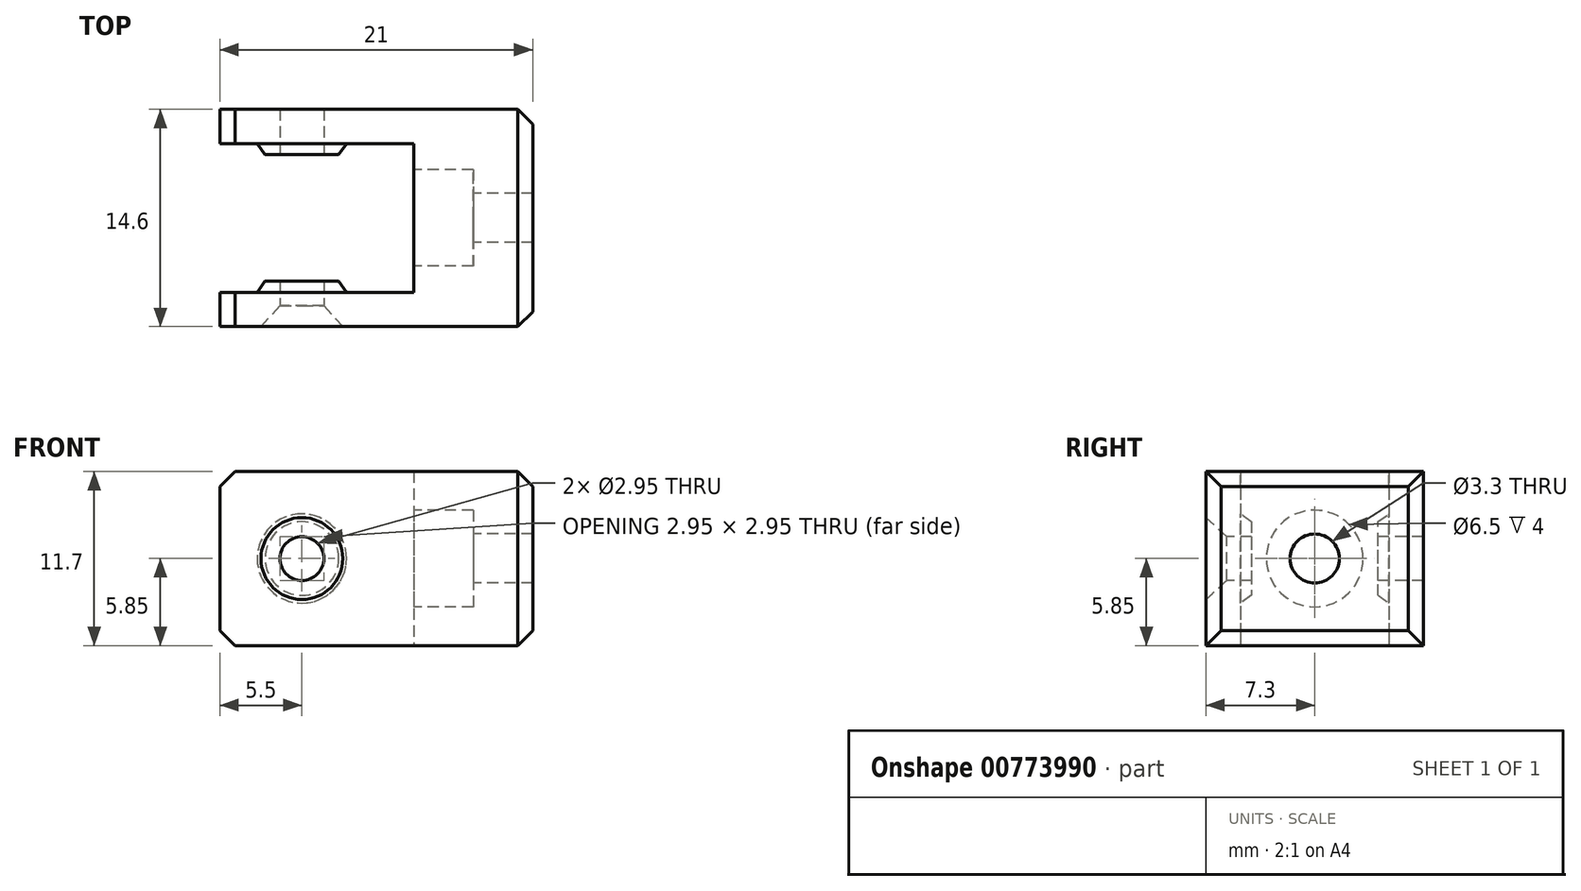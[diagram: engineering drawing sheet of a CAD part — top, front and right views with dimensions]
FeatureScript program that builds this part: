
annotation { "Feature Type Name" : "Feature", "Feature Type Description" : "" }
export const myFeature = defineFeature(function(context is Context, id is Id, definition is map)
    precondition{}
    {
        {
            var Q0;
            Q0=qCreatedBy(makeId("Top.planeOp"),FACE);
            var sketch = newSketch(context, id + "F0", { "sketchPlane" : qUnion([Q0])});
            skLineSegment(sketch, "E0", {"start": v(8, -7.3) * mm, "end": v(8, 0) * mm});
            skLineSegment(sketch, "E1", {"start": v(8, 0) * mm, "end": v(0, 0) * mm});
            skLineSegment(sketch, "E2", {"start": v(0, 0) * mm, "end": v(0, -5) * mm});
            skLineSegment(sketch, "E3", {"start": v(0, -5) * mm, "end": v(-13, -5) * mm});
            skLineSegment(sketch, "E4", {"start": v(-13, -5) * mm, "end": v(-13, -7.3) * mm});
            skLineSegment(sketch, "E5", {"start": v(-13, -7.3) * mm, "end": v(8, -7.3) * mm});
            skLineSegment(sketch, "E6.MirrorCS", {"start": v(0, 0) * mm, "end": v(0, 5) * mm});
            skLineSegment(sketch, "E7.MirrorCS", {"start": v(-13, 7.3) * mm, "end": v(8, 7.3) * mm});
            skLineSegment(sketch, "E8.MirrorCS", {"start": v(8, 7.3) * mm, "end": v(8, 0) * mm});
            skLineSegment(sketch, "E9.MirrorCS", {"start": v(0, 5) * mm, "end": v(-13, 5) * mm});
            skLineSegment(sketch, "E10.MirrorCS", {"start": v(-13, 5) * mm, "end": v(-13, 7.3) * mm});
            skSolve(sketch);
        }
        {
            var Q0;
            Q0 = qSketchRegion(id + "F0", true);
            extrude(context, id + "F1", {"entities" : qUnion([Q0]), "depth" : 11.7 * mm, "offsetDistance" : 25 * mm});
        }
        {
            var Q0;
            Q0=makeQuery(id+"F1.opExtrude","SWEPT_FACE",FACE,{"disambiguationData":[OSD([sQuery(id+"F0.wireOp",EDGE,"E5")])]});
            var sketch = newSketch(context, id + "F2", { "sketchPlane" : qUnion([Q0])});
            skLineSegment(sketch, "E11", {"start": v(-7.5, 11.7) * mm, "end": v(-7.5, 0) * mm});
            skPoint(sketch, "E12", {"position": v(-7.5, 5.85) * mm});
            skSolve(sketch);
        }
        {
            var Q0;
            Q0=makeQuery(id+"F1.opExtrude","SWEPT_FACE",FACE,{"disambiguationData":[OSD([sQuery(id+"F0.wireOp",EDGE,"E2"),sQuery(id+"F0.wireOp",EDGE,"E6.MirrorCS")])]});
            var sketch = newSketch(context, id + "F3", { "sketchPlane" : qUnion([Q0])});
            skLineSegment(sketch, "E13", {"start": v(0, 0) * mm, "end": v(0, 11.7) * mm});
            skPoint(sketch, "E14", {"position": v(0, 5.85) * mm});
            skSolve(sketch);
        }
        {
            var Q0;
            Q0=makeQuery(id+"F1.opExtrude","SWEPT_FACE",FACE,{"disambiguationData":[OSD([sQuery(id+"F0.wireOp",EDGE,"E3")])]});
            var sketch = newSketch(context, id + "F4", { "sketchPlane" : qUnion([Q0])});
            skCircle(sketch, "E15", {"center": v(7.5, 5.85) * mm, "radius": 3 * mm});
            skSolve(sketch);
        }
        {
            var Q0;
            Q0=makeQuery(id+"F1.opExtrude","SWEPT_FACE",FACE,{"disambiguationData":[OSD([sQuery(id+"F0.wireOp",EDGE,"E9.MirrorCS")])]});
            var sketch = newSketch(context, id + "F5", { "sketchPlane" : qUnion([Q0])});
            skCircle(sketch, "E16", {"center": v(-7.5, 5.85) * mm, "radius": 3 * mm});
            skSolve(sketch);
        }
        {
            var Q0;
            Q0 = qSketchRegion(id + "F4", true);
            extrude(context, id + "F6", {"entities" : qUnion([Q0]), "operationType" : NewBodyOperationType.ADD, "depth" : 0.75 * mm, "offsetDistance" : 25 * mm, "hasDraft" : true, "draftAngle" : 35 * degree, "draftPullDirection" : true});
        }
        {
            var Q0;
            Q0 = qSketchRegion(id + "F5", true);
            extrude(context, id + "F7", {"entities" : qUnion([Q0]), "operationType" : NewBodyOperationType.ADD, "depth" : 0.75 * mm, "offsetDistance" : 25 * mm, "hasDraft" : true, "draftAngle" : 35 * degree, "draftPullDirection" : true});
        }
        {
            var Q0;
            Q0=sQuery(id+"F2.wireOp",VERTEX,"E12");
            var Q1;
            Q1=makeQuery(id+"F1.opExtrude","SWEPT_BODY",BODY,{"disambiguationData":[OSD([sQuery(id+"F0.wireOp",EDGE,"E0"),sQuery(id+"F0.wireOp",EDGE,"E2"),sQuery(id+"F0.wireOp",EDGE,"E3"),sQuery(id+"F0.wireOp",EDGE,"E4"),sQuery(id+"F0.wireOp",EDGE,"E5"),sQuery(id+"F0.wireOp",EDGE,"E6.MirrorCS"),sQuery(id+"F0.wireOp",EDGE,"E7.MirrorCS"),sQuery(id+"F0.wireOp",EDGE,"E8.MirrorCS"),sQuery(id+"F0.wireOp",EDGE,"E9.MirrorCS"),sQuery(id+"F0.wireOp",EDGE,"E10.MirrorCS")])]});
            hole(context, id + "F8", {"style" : HoleStyle.C_SINK, "endStyle" : HoleEndStyle.THROUGH, "holeDiameter" : 2.95 * mm, "cSinkDiameter" : 5.5 * mm, "cSinkAngle" : 85 * degree, "majorDiameter" : 3 * mm, "isTappedThrough" : true, "tappedDepth" : 12 * mm, "tapClearance" : 3, "locations" : qUnion([Q0]), "scope" : qUnion([Q1])});
        }
        {
            var Q0;
            Q0=sQuery(id+"F3.wireOp",VERTEX,"E14");
            var Q1;
            Q1=makeQuery(id+"F1.opExtrude","SWEPT_BODY",BODY,{"disambiguationData":[OSD([sQuery(id+"F0.wireOp",EDGE,"E0"),sQuery(id+"F0.wireOp",EDGE,"E2"),sQuery(id+"F0.wireOp",EDGE,"E3"),sQuery(id+"F0.wireOp",EDGE,"E4"),sQuery(id+"F0.wireOp",EDGE,"E5"),sQuery(id+"F0.wireOp",EDGE,"E6.MirrorCS"),sQuery(id+"F0.wireOp",EDGE,"E7.MirrorCS"),sQuery(id+"F0.wireOp",EDGE,"E8.MirrorCS"),sQuery(id+"F0.wireOp",EDGE,"E9.MirrorCS"),sQuery(id+"F0.wireOp",EDGE,"E10.MirrorCS")])]});
            hole(context, id + "F9", {"style" : HoleStyle.C_BORE, "endStyle" : HoleEndStyle.THROUGH, "holeDiameter" : 3.3 * mm, "cBoreDiameter" : 6.5 * mm, "cBoreDepth" : 4 * mm, "majorDiameter" : 5 * mm, "isTappedThrough" : true, "tappedDepth" : 12 * mm, "tapClearance" : 3, "locations" : qUnion([Q0]), "scope" : qUnion([Q1])});
        }
        {
            var Q0;
            Q0=makeQuery(id+"F1.opExtrude","CAP_EDGE",EDGE,{"disambiguationData":[OSD([sQuery(id+"F0.wireOp",EDGE,"E4")])],"isStart":false});
            var Q1;
            Q1=makeQuery(id+"F1.opExtrude","CAP_EDGE",EDGE,{"disambiguationData":[OSD([sQuery(id+"F0.wireOp",EDGE,"E4")])],"isStart":true});
            var Q2;
            Q2=makeQuery(id+"F1.opExtrude","CAP_EDGE",EDGE,{"disambiguationData":[OSD([sQuery(id+"F0.wireOp",EDGE,"E10.MirrorCS")])],"isStart":true});
            var Q3;
            Q3=makeQuery(id+"F1.opExtrude","CAP_EDGE",EDGE,{"disambiguationData":[OSD([sQuery(id+"F0.wireOp",EDGE,"E10.MirrorCS")])],"isStart":false});
            var Q4;
            Q4=makeQuery(id+"F1.opExtrude","CAP_EDGE",EDGE,{"disambiguationData":[OSD([sQuery(id+"F0.wireOp",EDGE,"E0"),sQuery(id+"F0.wireOp",EDGE,"E8.MirrorCS")])],"isStart":false});
            var Q5;
            Q5=makeQuery(id+"F1.opExtrude","SWEPT_EDGE",EDGE,{"disambiguationData":[OSD([sQuery(id+"F0.wireOp",EDGE,"E0"),sQuery(id+"F0.wireOp",EDGE,"E5")])]});
            var Q6;
            Q6=makeQuery(id+"F1.opExtrude","CAP_EDGE",EDGE,{"disambiguationData":[OSD([sQuery(id+"F0.wireOp",EDGE,"E0"),sQuery(id+"F0.wireOp",EDGE,"E8.MirrorCS")])],"isStart":true});
            var Q7;
            Q7=makeQuery(id+"F1.opExtrude","SWEPT_EDGE",EDGE,{"disambiguationData":[OSD([sQuery(id+"F0.wireOp",EDGE,"E7.MirrorCS"),sQuery(id+"F0.wireOp",EDGE,"E8.MirrorCS")])]});
            chamfer(context, id + "F10", {"entities" : qUnion([Q0, Q1, Q2, Q3, Q4, Q5, Q6, Q7]), "width" : 1 * mm, "tangentPropagation" : true});
        }
    });
